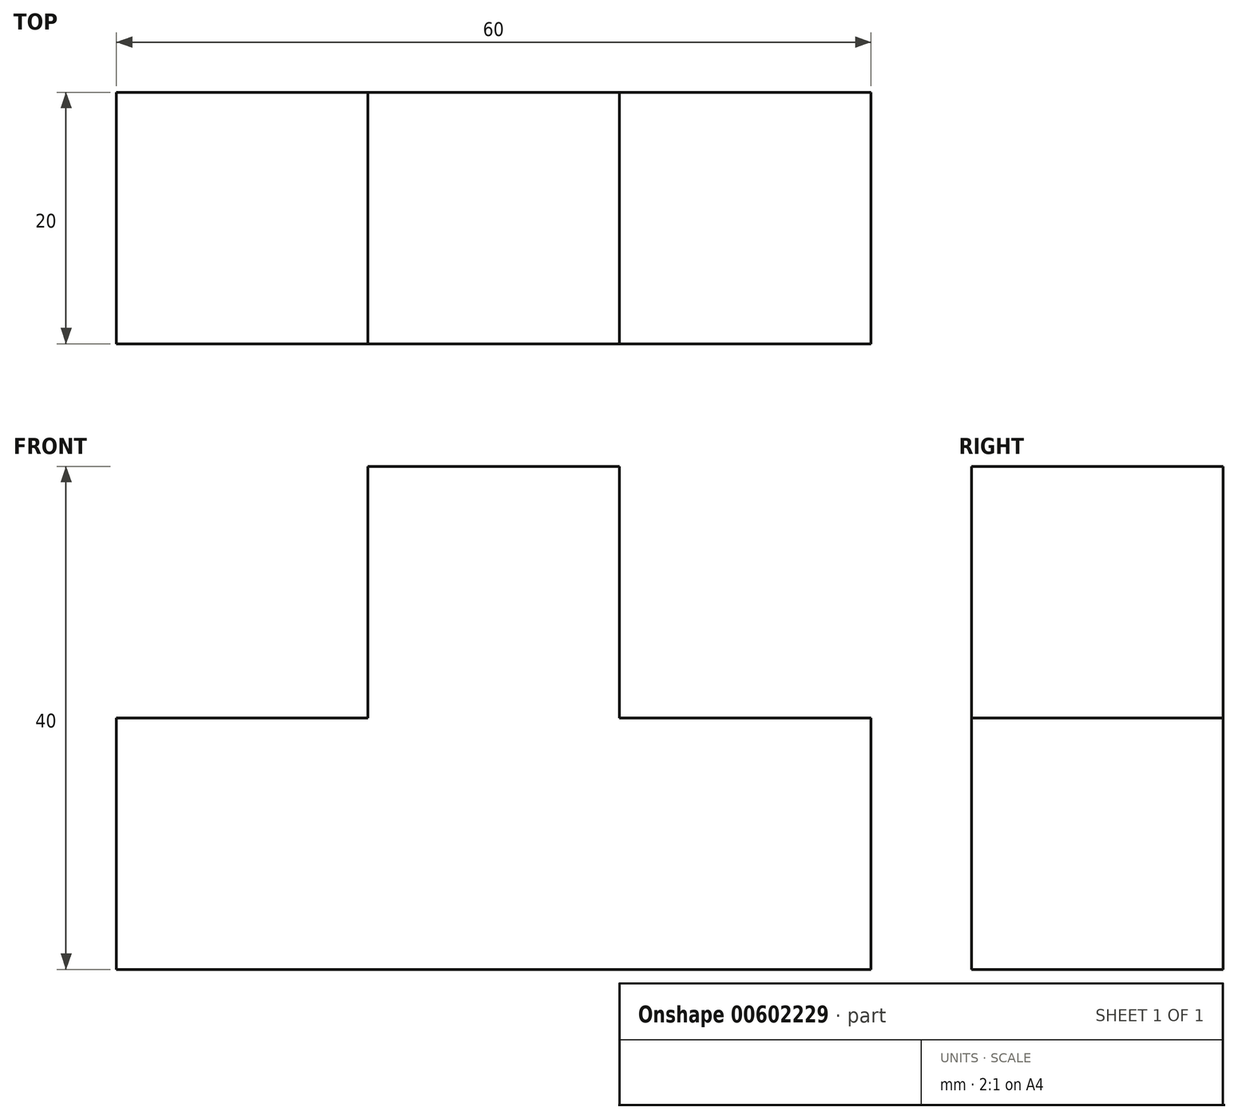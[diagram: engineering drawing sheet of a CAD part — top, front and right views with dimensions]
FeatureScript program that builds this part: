
annotation { "Feature Type Name" : "Feature", "Feature Type Description" : "" }
export const myFeature = defineFeature(function(context is Context, id is Id, definition is map)
    precondition{}
    {
        {
            var Q0;
            Q0=qCreatedBy(makeId("Front.planeOp"),FACE);
            var sketch = newSketch(context, id + "F0", { "sketchPlane" : qUnion([Q0])});
            skLineSegment(sketch, "E0", {"start": v(-8.61, 28.35) * mm, "end": v(11.39, 28.35) * mm});
            skLineSegment(sketch, "E1", {"start": v(11.39, 28.35) * mm, "end": v(11.39, 8.35) * mm});
            skLineSegment(sketch, "E2", {"start": v(11.39, 8.35) * mm, "end": v(31.39, 8.35) * mm});
            skLineSegment(sketch, "E3", {"start": v(31.39, 8.35) * mm, "end": v(31.39, -11.65) * mm});
            skLineSegment(sketch, "E4", {"start": v(31.39, -11.65) * mm, "end": v(-28.61, -11.65) * mm});
            skLineSegment(sketch, "E5", {"start": v(-28.61, -11.65) * mm, "end": v(-28.61, 8.35) * mm});
            skLineSegment(sketch, "E6", {"start": v(-28.61, 8.35) * mm, "end": v(-8.61, 8.35) * mm});
            skLineSegment(sketch, "E7", {"start": v(-8.61, 8.35) * mm, "end": v(-8.61, 28.35) * mm});
            skSolve(sketch);
        }
        {
            var Q0;
            Q0 = qSketchRegion(id + "F0", true);
            extrude(context, id + "F1", {"entities" : qUnion([Q0]), "depth" : 20 * mm, "offsetDistance" : 25 * mm});
        }
    });
